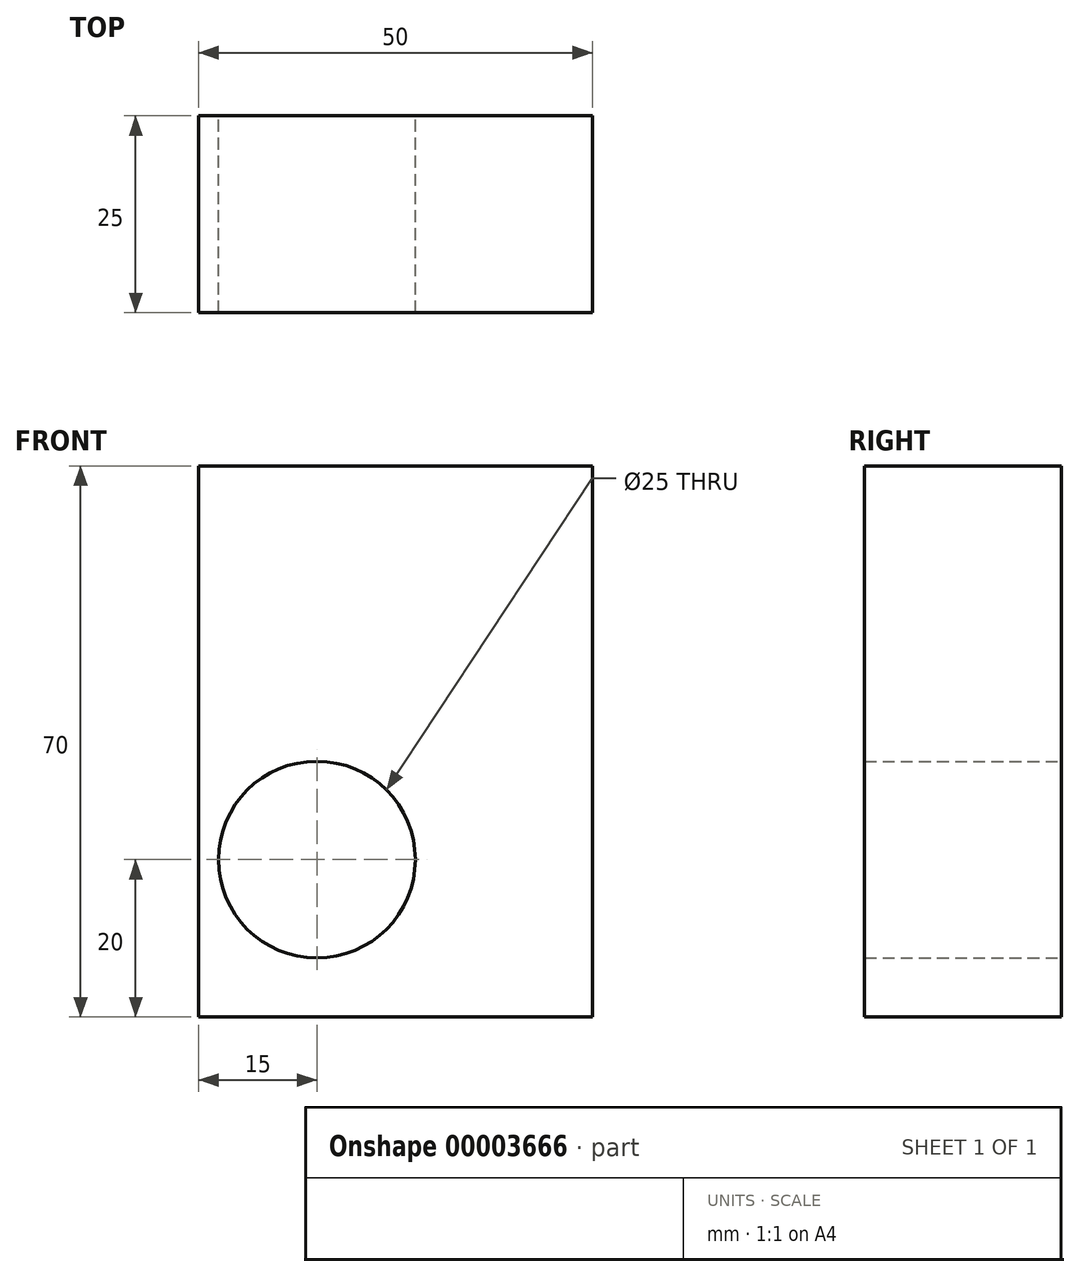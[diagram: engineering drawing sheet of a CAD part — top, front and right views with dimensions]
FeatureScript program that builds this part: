
annotation { "Feature Type Name" : "Feature", "Feature Type Description" : "" }
export const myFeature = defineFeature(function(context is Context, id is Id, definition is map)
    precondition{}
    {
        {
            var Q0;
            Q0=qCreatedBy(makeId("Front.planeOp"),FACE);
            var sketch = newSketch(context, id + "F0", { "sketchPlane" : qUnion([Q0])});
            skLineSegment(sketch, "E0.bottom", {"start": v(-15, 50) * mm, "end": v(35, 50) * mm});
            skLineSegment(sketch, "E0.top", {"start": v(-15, -20) * mm, "end": v(35, -20) * mm});
            skLineSegment(sketch, "E0.left", {"start": v(-15, 50) * mm, "end": v(-15, -20) * mm});
            skLineSegment(sketch, "E0.right", {"start": v(35, 50) * mm, "end": v(35, -20) * mm});
            skCircle(sketch, "E1", {"center": v(0, 0) * mm, "radius": 12.5 * mm});
            skSolve(sketch);
        }
        {
            var Q0;
            Q0 = qSketchRegion(id + "F0", true);
            extrude(context, id + "F1", {"entities" : qUnion([Q0]), "depth" : 25 * mm});
        }
    });
